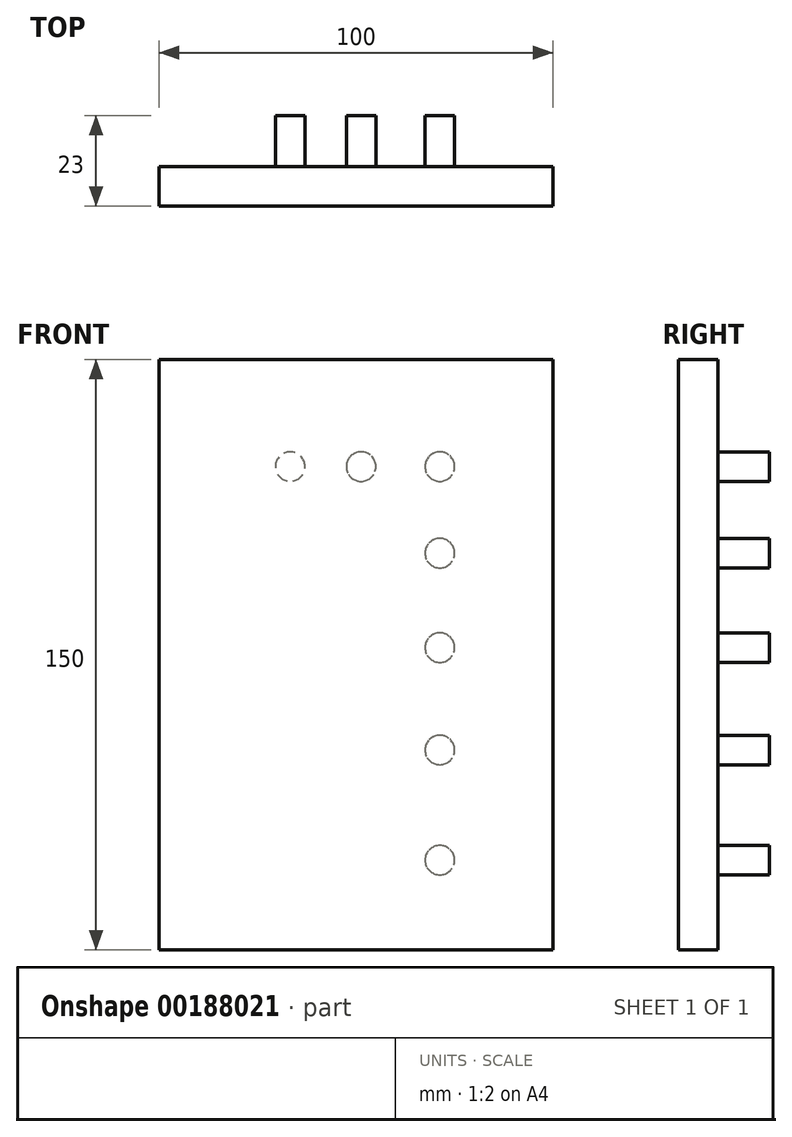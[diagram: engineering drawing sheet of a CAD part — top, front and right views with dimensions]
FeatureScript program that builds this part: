
annotation { "Feature Type Name" : "Feature", "Feature Type Description" : "" }
export const myFeature = defineFeature(function(context is Context, id is Id, definition is map)
    precondition{}
    {
        {
            var Q0;
            Q0=qCreatedBy(makeId("Front.planeOp"),FACE);
            var sketch = newSketch(context, id + "F0", { "sketchPlane" : qUnion([Q0])});
            skLineSegment(sketch, "E0.bottom", {"start": v(-46.92, 108.03) * mm, "end": v(53.08, 108.03) * mm});
            skLineSegment(sketch, "E0.top", {"start": v(-46.92, -41.97) * mm, "end": v(53.08, -41.97) * mm});
            skLineSegment(sketch, "E0.left", {"start": v(-46.92, 108.03) * mm, "end": v(-46.92, -41.97) * mm});
            skLineSegment(sketch, "E0.right", {"start": v(53.08, 108.03) * mm, "end": v(53.08, -41.97) * mm});
            skSolve(sketch);
        }
        {
            var Q0;
            Q0=makeQuery(id+"F0.imprint","IMPRINT",FACE,{"disambiguationData":[TD([[makeQuery(id+"F0.imprint","IMPRINT",EDGE,{"derivedFrom":sQuery(id+"F0.wireOp",EDGE,"E0.bottom")}),-1.0]])]});
            var Q1;
            Q1=qSketchRegion(id+"FP9mmCFv8DciCVo_1",true);
            var Q2;
            Q2=sQuery(id+"F0.wireOp",EDGE,"E0.right");
            var Q3;
            Q3=sQuery(id+"F0.wireOp",EDGE,"E0.bottom");
            var Q4;
            Q4=sQuery(id+"F0.wireOp",EDGE,"E0.top");
            var Q5;
            Q5=sQuery(id+"F0.wireOp",EDGE,"E0.left");
            extrude(context, id + "F1", {"entities" : qUnion([Q0, Q1]), "surfaceEntities" : qUnion([Q2, Q3, Q4, Q5]), "depth" : 10 * mm});
        }
        {
            var Q0;
            Q0=makeQuery(id+"F1.opExtrude","CAP_FACE",FACE,{"disambiguationData":[OSD([sQuery(id+"F0.wireOp",EDGE,"E0.bottom"),sQuery(id+"F0.wireOp",EDGE,"E0.top"),sQuery(id+"F0.wireOp",EDGE,"E0.left"),sQuery(id+"F0.wireOp",EDGE,"E0.right")])],"isStart":true});
            var sketch = newSketch(context, id + "F2", { "sketchPlane" : qUnion([Q0])});
            skCircle(sketch, "E1", {"center": v(13.61, 80.84) * mm, "radius": 3.75 * mm});
            skCircle(sketch, "E2", {"center": v(-4.39, 80.84) * mm, "radius": 3.75 * mm});
            skCircle(sketch, "E3", {"center": v(-24.39, 80.84) * mm, "radius": 3.75 * mm});
            skCircle(sketch, "E4", {"center": v(-24.39, 58.84) * mm, "radius": 3.75 * mm});
            skCircle(sketch, "E5", {"center": v(-24.39, 34.84) * mm, "radius": 3.75 * mm});
            skCircle(sketch, "E6", {"center": v(-24.39, 8.84) * mm, "radius": 3.75 * mm});
            skCircle(sketch, "E7", {"center": v(-24.39, -19.16) * mm, "radius": 3.75 * mm});
            skSolve(sketch);
        }
        {
            var Q0;
            Q0=qSketchRegion(id+"F2",true);
            extrude(context, id + "F3", {"entities" : qUnion([Q0]), "operationType" : NewBodyOperationType.ADD, "depth" : 13 * mm});
        }
    });
